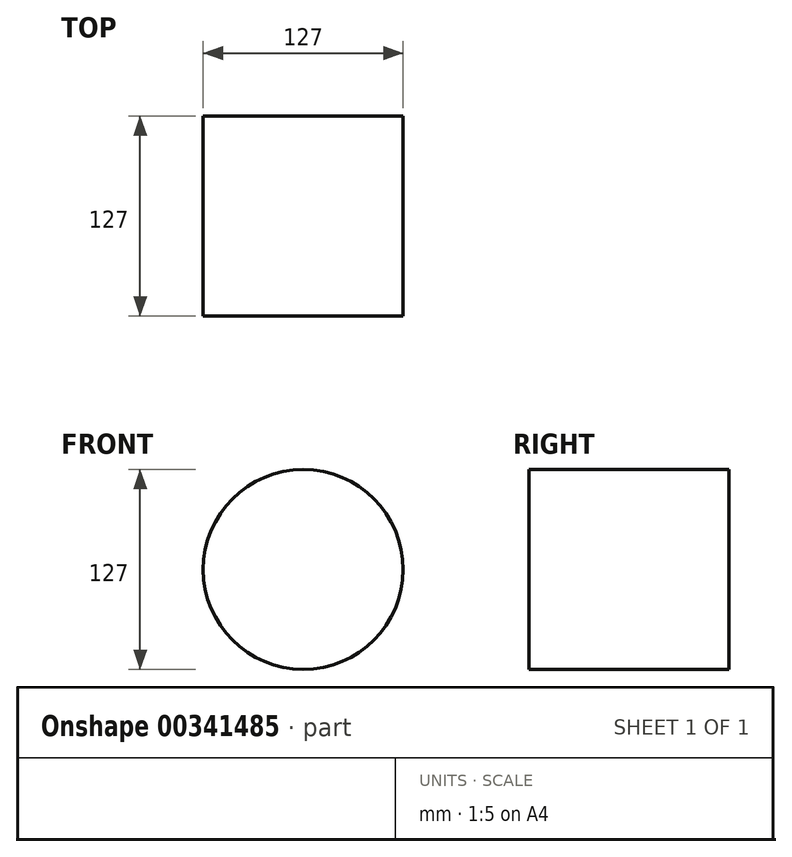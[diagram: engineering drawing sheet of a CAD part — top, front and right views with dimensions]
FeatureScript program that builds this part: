
annotation { "Feature Type Name" : "Feature", "Feature Type Description" : "" }
export const myFeature = defineFeature(function(context is Context, id is Id, definition is map)
    precondition{}
    {
        {
            var Q0;
            Q0=qCreatedBy(makeId("Front.planeOp"),FACE);
            var sketch = newSketch(context, id + "F0", { "sketchPlane" : qUnion([Q0])});
            skCircle(sketch, "E0", {"center": v(0, 0) * mm, "radius": 63.5 * mm});
            skSolve(sketch);
        }
        {
            var Q0;
            Q0 = qSketchRegion(id + "F0", true);
            extrude(context, id + "F1", {"entities" : qUnion([Q0]), "endBound" : BoundingType.SYMMETRIC, "depth" : 127 * mm});
        }
    });
